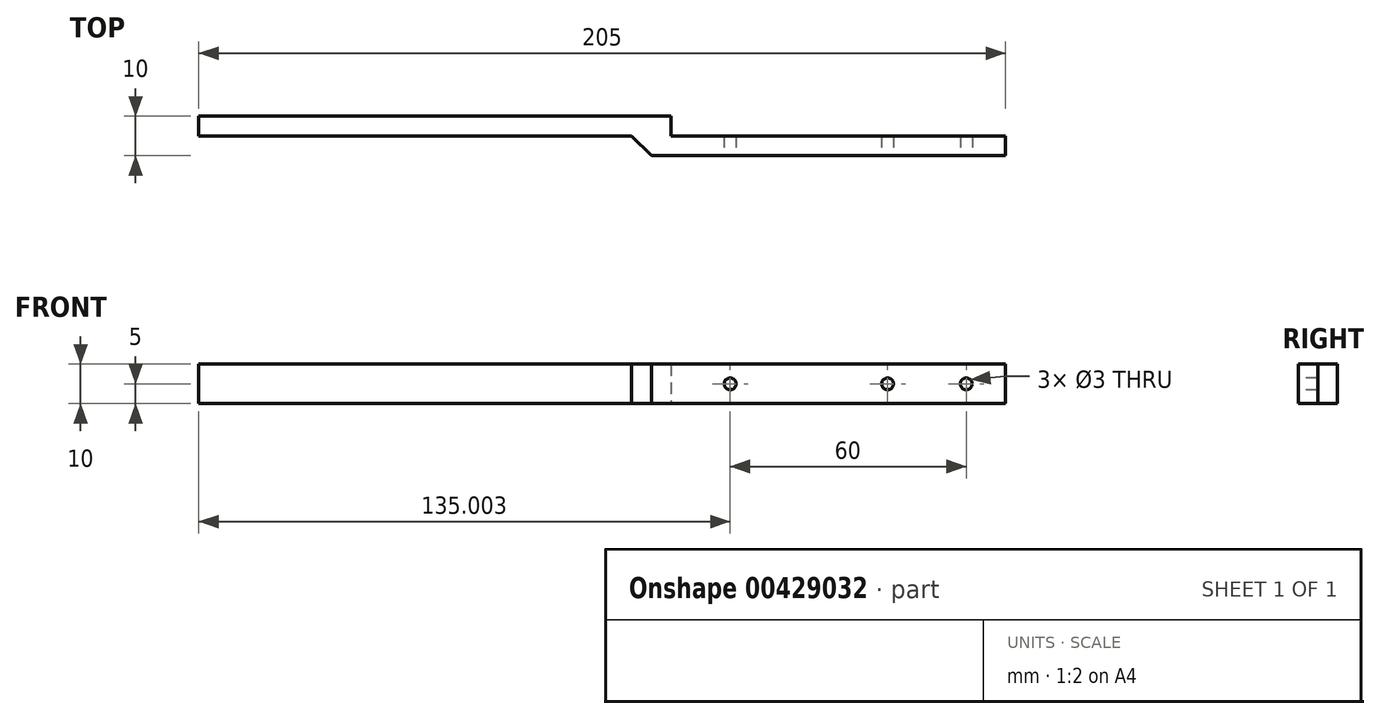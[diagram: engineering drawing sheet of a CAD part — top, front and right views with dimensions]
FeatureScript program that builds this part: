
annotation { "Feature Type Name" : "Feature", "Feature Type Description" : "" }
export const myFeature = defineFeature(function(context is Context, id is Id, definition is map)
    precondition{}
    {
        {
            var Q0;
            Q0=qCreatedBy(makeId("Top.planeOp"),FACE);
            var sketch = newSketch(context, id + "F0", { "sketchPlane" : qUnion([Q0])});
            skLineSegment(sketch, "E0", {"start": v(-106.64, 15.18) * mm, "end": v(13.36, 15.18) * mm});
            skLineSegment(sketch, "E1", {"start": v(13.36, 15.18) * mm, "end": v(13.36, 10.18) * mm});
            skLineSegment(sketch, "E2", {"start": v(13.36, 10.18) * mm, "end": v(98.36, 10.18) * mm});
            skLineSegment(sketch, "E3.0", {"start": v(-106.64, 10.18) * mm, "end": v(3.36, 10.18) * mm});
            skLineSegment(sketch, "E4.0", {"start": v(13.36, 5.18) * mm, "end": v(98.36, 5.18) * mm});
            skLineSegment(sketch, "E5", {"start": v(13.36, 5.18) * mm, "end": v(8.36, 5.18) * mm});
            skLineSegment(sketch, "E6", {"start": v(98.36, 10.18) * mm, "end": v(98.36, 5.18) * mm});
            skPoint(sketch, "E7.orphan", {"position": v(0, 5.18) * mm});
            skLineSegment(sketch, "E8", {"start": v(-106.64, 15.18) * mm, "end": v(-106.64, 10.18) * mm});
            skLineSegment(sketch, "E9", {"start": v(8.36, 5.18) * mm, "end": v(3.36, 10.18) * mm});
            skSolve(sketch);
        }
        {
            var Q0;
            Q0=makeQuery(id+"F0.imprint","IMPRINT",FACE,{"disambiguationData":[TD([[makeQuery(id+"F0.imprint","IMPRINT",EDGE,{"derivedFrom":sQuery(id+"F0.wireOp",EDGE,"E0")}),-1.0]])]});
            extrude(context, id + "F1", {"entities" : qUnion([Q0]), "depth" : 10 * mm});
        }
        {
            var Q0;
            Q0=makeQuery(id+"F1.opExtrude","SWEPT_FACE",FACE,{"disambiguationData":[OSD([sQuery(id+"F0.wireOp",EDGE,"E4.0"),sQuery(id+"F0.wireOp",EDGE,"E5")])]});
            var sketch = newSketch(context, id + "F2", { "sketchPlane" : qUnion([Q0])});
            skCircle(sketch, "E10", {"center": v(88.36, 5) * mm, "radius": 1.5 * mm});
            skCircle(sketch, "E11", {"center": v(68.36, 5) * mm, "radius": 1.5 * mm});
            skCircle(sketch, "E12", {"center": v(28.36, 5) * mm, "radius": 1.5 * mm});
            skSolve(sketch);
        }
        {
            var Q0;
            Q0=makeQuery(id+"F2.imprint","IMPRINT",FACE,{"disambiguationData":[TD([[makeQuery(id+"F2.imprint","IMPRINT",EDGE,{"derivedFrom":sQuery(id+"F2.wireOp",EDGE,"E10")}),1.0]])]});
            var Q1;
            Q1=makeQuery(id+"F2.imprint","IMPRINT",FACE,{"disambiguationData":[TD([[makeQuery(id+"F2.imprint","IMPRINT",EDGE,{"derivedFrom":sQuery(id+"F2.wireOp",EDGE,"E11")}),1.0]])]});
            var Q2;
            Q2=makeQuery(id+"F2.imprint","IMPRINT",FACE,{"disambiguationData":[TD([[makeQuery(id+"F2.imprint","IMPRINT",EDGE,{"derivedFrom":sQuery(id+"F2.wireOp",EDGE,"E12")}),1.0]])]});
            extrude(context, id + "F3", {"entities" : qUnion([Q0, Q1, Q2]), "operationType" : NewBodyOperationType.REMOVE, "endBound" : BoundingType.THROUGH_ALL, "oppositeDirection" : true, "depth" : 25 * mm});
        }
    });
